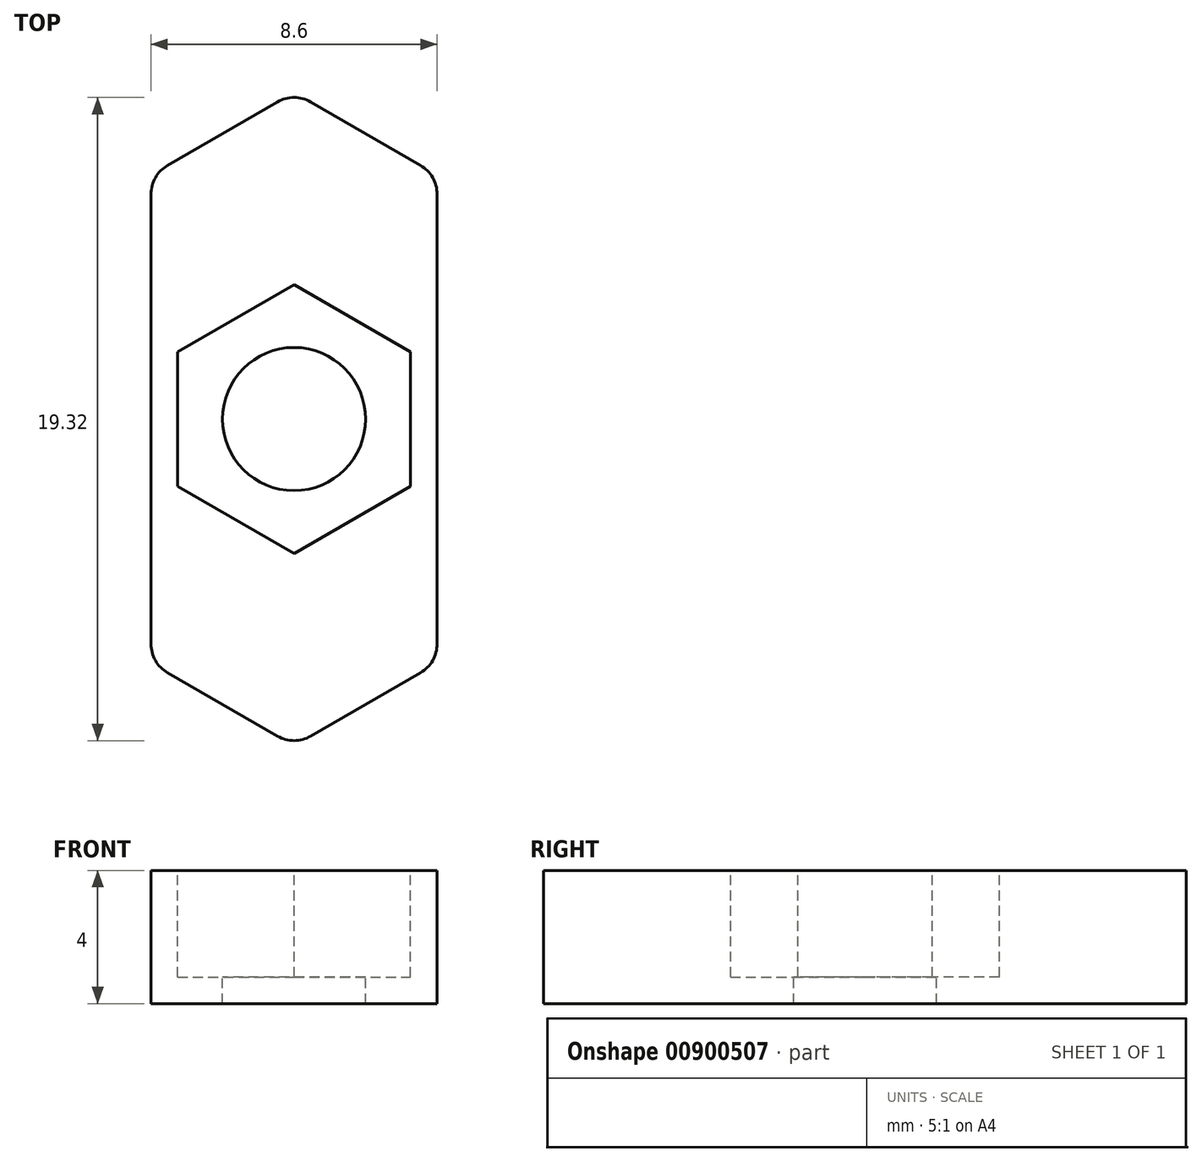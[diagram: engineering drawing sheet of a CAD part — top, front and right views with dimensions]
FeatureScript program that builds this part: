
annotation { "Feature Type Name" : "Feature", "Feature Type Description" : "" }
export const myFeature = defineFeature(function(context is Context, id is Id, definition is map)
    precondition{}
    {
        {
            var Q0;
            Q0=qCreatedBy(makeId("Top.planeOp"),FACE);
            var sketch = newSketch(context, id + "F0", { "sketchPlane" : qUnion([Q0])});
            skCircle(sketch, "E0", {"center": v(0, 0) * mm, "radius": 2.15 * mm});
            skCircle(sketch, "E1.cCircle", {"center": v(0, 0) * mm, "radius": 3.5 * mm, "construction": true});
            skLineSegment(sketch, "E1.0", {"start": v(3.5, 2.02) * mm, "end": v(3.5, -2.02) * mm});
            skLineSegment(sketch, "E1.1", {"start": v(3.5, -2.02) * mm, "end": v(0, -4.04) * mm});
            skLineSegment(sketch, "E1.2", {"start": v(0, -4.04) * mm, "end": v(-3.5, -2.02) * mm});
            skLineSegment(sketch, "E1.3", {"start": v(-3.5, -2.02) * mm, "end": v(-3.5, 2.02) * mm});
            skLineSegment(sketch, "E1.4", {"start": v(-3.5, 2.02) * mm, "end": v(0, 4.04) * mm});
            skLineSegment(sketch, "E1.5", {"start": v(0, 4.04) * mm, "end": v(3.5, 2.02) * mm});
            skPoint(sketch, "E1.0.midPoint", {"position": v(3.5, 0) * mm});
            skLineSegment(sketch, "E2", {"start": v(0, -4.04) * mm, "end": v(0, 4.04) * mm, "construction": true});
            skLineSegment(sketch, "E3.0", {"start": v(4.3, 7.33) * mm, "end": v(4.3, -7.33) * mm});
            skLineSegment(sketch, "E4.0", {"start": v(0, 9.81) * mm, "end": v(4.3, 7.33) * mm});
            skLineSegment(sketch, "E5.0", {"start": v(4.3, -7.33) * mm, "end": v(0, -9.81) * mm});
            skLineSegment(sketch, "E6.MirrorCS", {"start": v(0, 9.81) * mm, "end": v(-4.3, 7.33) * mm});
            skLineSegment(sketch, "E7.MirrorCS", {"start": v(-4.3, 7.33) * mm, "end": v(-4.3, -7.33) * mm});
            skLineSegment(sketch, "E8.MirrorCS", {"start": v(-4.3, -7.33) * mm, "end": v(0, -9.81) * mm});
            skSolve(sketch);
        }
        {
            var Q0;
            Q0=makeQuery(id+"F0.imprint","IMPRINT",FACE,{"disambiguationData":[TD([[makeQuery(id+"F0.imprint","IMPRINT",EDGE,{"derivedFrom":sQuery(id+"F0.wireOp",EDGE,"E1.0")}),1.0]])]});
            var Q1;
            Q1=makeQuery(id+"F0.imprint","IMPRINT",FACE,{"disambiguationData":[TD([[makeQuery(id+"F0.imprint","IMPRINT",EDGE,{"derivedFrom":sQuery(id+"F0.wireOp",EDGE,"E0")}),-1.0]])]});
            extrude(context, id + "F1", {"entities" : qUnion([Q0, Q1]), "oppositeDirection" : true, "depth" : 4 * mm, "offsetDistance" : 25 * mm});
        }
        {
            var Q0;
            Q0=makeQuery(id+"F0.imprint","IMPRINT",FACE,{"disambiguationData":[TD([[makeQuery(id+"F0.imprint","IMPRINT",EDGE,{"derivedFrom":sQuery(id+"F0.wireOp",EDGE,"E0")}),-1.0]])]});
            extrude(context, id + "F2", {"entities" : qUnion([Q0]), "operationType" : NewBodyOperationType.REMOVE, "oppositeDirection" : true, "depth" : 3.2 * mm, "offsetDistance" : 25 * mm});
        }
        {
            var Q0;
            Q0=makeQuery(id+"F1.opExtrude","SWEPT_EDGE",EDGE,{"disambiguationData":[OSD([sQuery(id+"F0.wireOp",EDGE,"E6.MirrorCS"),sQuery(id+"F0.wireOp",EDGE,"E7.MirrorCS")])]});
            var Q1;
            Q1=makeQuery(id+"F1.opExtrude","SWEPT_EDGE",EDGE,{"disambiguationData":[OSD([sQuery(id+"F0.wireOp",EDGE,"E4.0"),sQuery(id+"F0.wireOp",EDGE,"E6.MirrorCS")])]});
            var Q2;
            Q2=makeQuery(id+"F1.opExtrude","SWEPT_EDGE",EDGE,{"disambiguationData":[OSD([sQuery(id+"F0.wireOp",EDGE,"E3.0"),sQuery(id+"F0.wireOp",EDGE,"E4.0")])]});
            var Q3;
            Q3=makeQuery(id+"F1.opExtrude","SWEPT_EDGE",EDGE,{"disambiguationData":[OSD([sQuery(id+"F0.wireOp",EDGE,"E3.0"),sQuery(id+"F0.wireOp",EDGE,"E5.0")])]});
            var Q4;
            Q4=makeQuery(id+"F1.opExtrude","SWEPT_EDGE",EDGE,{"disambiguationData":[OSD([sQuery(id+"F0.wireOp",EDGE,"E5.0"),sQuery(id+"F0.wireOp",EDGE,"E8.MirrorCS")])]});
            var Q5;
            Q5=makeQuery(id+"F1.opExtrude","SWEPT_EDGE",EDGE,{"disambiguationData":[OSD([sQuery(id+"F0.wireOp",EDGE,"E7.MirrorCS"),sQuery(id+"F0.wireOp",EDGE,"E8.MirrorCS")])]});
            fillet(context, id + "F3", {"entities" : qUnion([Q0, Q1, Q2, Q3, Q4, Q5]), "radius" : 1 * mm, "tangentPropagation" : true, "allowEdgeOverflow" : false});
        }
    });
